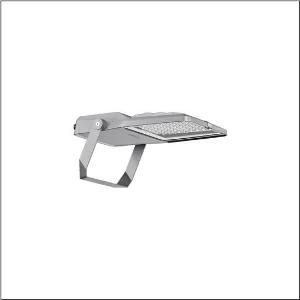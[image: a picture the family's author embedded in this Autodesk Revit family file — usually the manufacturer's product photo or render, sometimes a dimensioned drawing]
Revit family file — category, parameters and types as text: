
# Revit family: floodlight_fl_21_iq_mini___pl61_5xa7772c5c1a_22e4
name_source: partatom
category: Lighting Fixtures
units: mm (PartAtom-declared; Revit-internal decimal feet)

## family parameters
Cut with Voids When Loaded = No
Host = Face
Light Source = No
Part Type = Normal
Room Calculation Point = No
Round Connector Dimension = Use Diameter
Shared = No

## types (1)
- --- (1 x LED, 11180 lm, 87.2 W, 4000K)
    Apparent Load = 87 VA
    CIE Flux Codes = 33 65 98 100 100
    Color Rendering = 80
    Color Temperature = 4000K
    Default Elevation = 1800 mm
    Description = Floodlight FL 21 iQ mini, floodlight, primary light control with lens, of PMMA, primary optical cover: protective disc, of toughened safety glass, transparent, light distribution: PL61, light emission: direct distribution, installation type: surface-mounted, LED, High Power LED, rated luminous flux: 11.180lm, luminous efficacy: 128lm/W, light colour: 840, colour temperature: 4000K, control: Street-Remote, Auto-Match, Temp-Guard, Night-Set, Smart-Wire, Desk-Remote (wireless, voltage-free reading and setting of iQ features in the workshop via application-optimized NFC function/RFID function), optimised constant luminous flux control (CLO 2.0), with terminal, 6-pole, mains connection: 220..240V, AC, 50/60Hz, start of lifetime: 87W, end of service life: 92W, reduction: 40W, luminaire housing, of diecast aluminium, powder-coated, Siteco® metallic grey (DB 702S), corrosivity category C5 mid according to DIN EN ISO 12944, sealing non-destructively replaceable, mounting bracket, of steel, galvanised, powder-coated, Siteco® metallic grey (DB 702S), protection rating (complete): IP66, insulation class (complete): insulation class II (safety insulation), certification: CE, ENEC, VDE, protection symbol: D, impact resistance: IK08, permissible operating ambient temperature: -40..+40°C, permissible operating ambient temperature for outdoor applications: -40..+50°C, standard: DIN EN 12944, LABS conformity tested according to VDMA 24364:2018-05, packaging unit: 1 piece

Light Distribution: PL61
    Height = 70 mm
    Lamp = 1 x LED
    Lamp Light Flux = 11180 lm
    Lamp Power = 87.2 W
    Lamp count = 1
    Length = 485 mm
    Luminous efficacy = 128 lm/W
    Manufacturer = Siteco
    ModVariant = No
    Model = 5XA7772C5C1A
    Number of Poles = 1
    OnlyDefault = Yes
    Power Factor = 1
    Product Name = Floodlight FL 21 iQ mini | PL61
    Product group = floodlight | pylon annexe
    ProductGroupID = 6200
    Protection Class = Protection class II
    Protection Degree = IP 66
    RLX_Detail_Level = 1
    RLX_Emergency_Light_Flux = 0 lm
    RLX_Emergency_Type = 0
    RLX_Emergency_Type_DB = No
    RlxData = <blob elided: 96353 chars, md5=8a92ac90>
    Socket = socket
    Standby Power = 0 W
    System Light Flux = 11180 lm
    System Power = 87 W
    Type Comments = factory setting: luminous flux: 100 % | dim-lin: 254 | 456 mA
    Type Image = l_1006845.jpg
    URL = http://relux.com
    VarID = @adj_105939
    Voltage = 0 V
    Weight = 0.00 kg
    Width = 337 mm

## geometry (parser evidence)
native form markers: Blend x4, Sweep x13
no freeform markers — native parametric forms only
